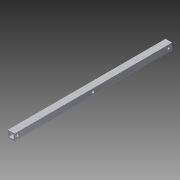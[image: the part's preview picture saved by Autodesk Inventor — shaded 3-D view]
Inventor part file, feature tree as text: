
AUTODESK INVENTOR PART (.ipt)
format: ipt  version: 2013 (Build 170138000, 138)  size: 114,176 bytes
history: native  units: in
note: dims shown in document units (in); Inventor stores cm internally (conversion verified against a paired STEP export)
features: sketch x3, extrude x2, hole x1
ambient origin geometry x8: Origin, YZ Plane, XZ Plane, XY Plane, X Axis, Y Axis, Z Axis, Center Point
bodies: Solid1 (feature_tree)
feature tree (6):
  extrude  "Extrusion1"  Depth=0.5in
  hole  "Hole1"  [1 undecoded]
  extrude  "Extrusion2"  Depth=0.168in
  sketch  "Sketch1"  dims[d0=0.5in d1=0.5in]
  sketch  "Sketch3"  dims[d3=12.0in d4=0.0in d5=0.07in]
  sketch  "Sketch4"  dims[d6=0.1875in d7=0.75in d8=0.375in d9=0.25in d10=0.5635in d11=1.0in d12=0.8108in d13=0.168in d14=0.25in d15=0.168in d16=0.25in d17=0.5in d18=0.0in]
note: 1 required parameter value undecoded (feature->parameter linkage not recoverable at this tier; creation-order binding heuristic only, values carry confidence <= 0.55)
